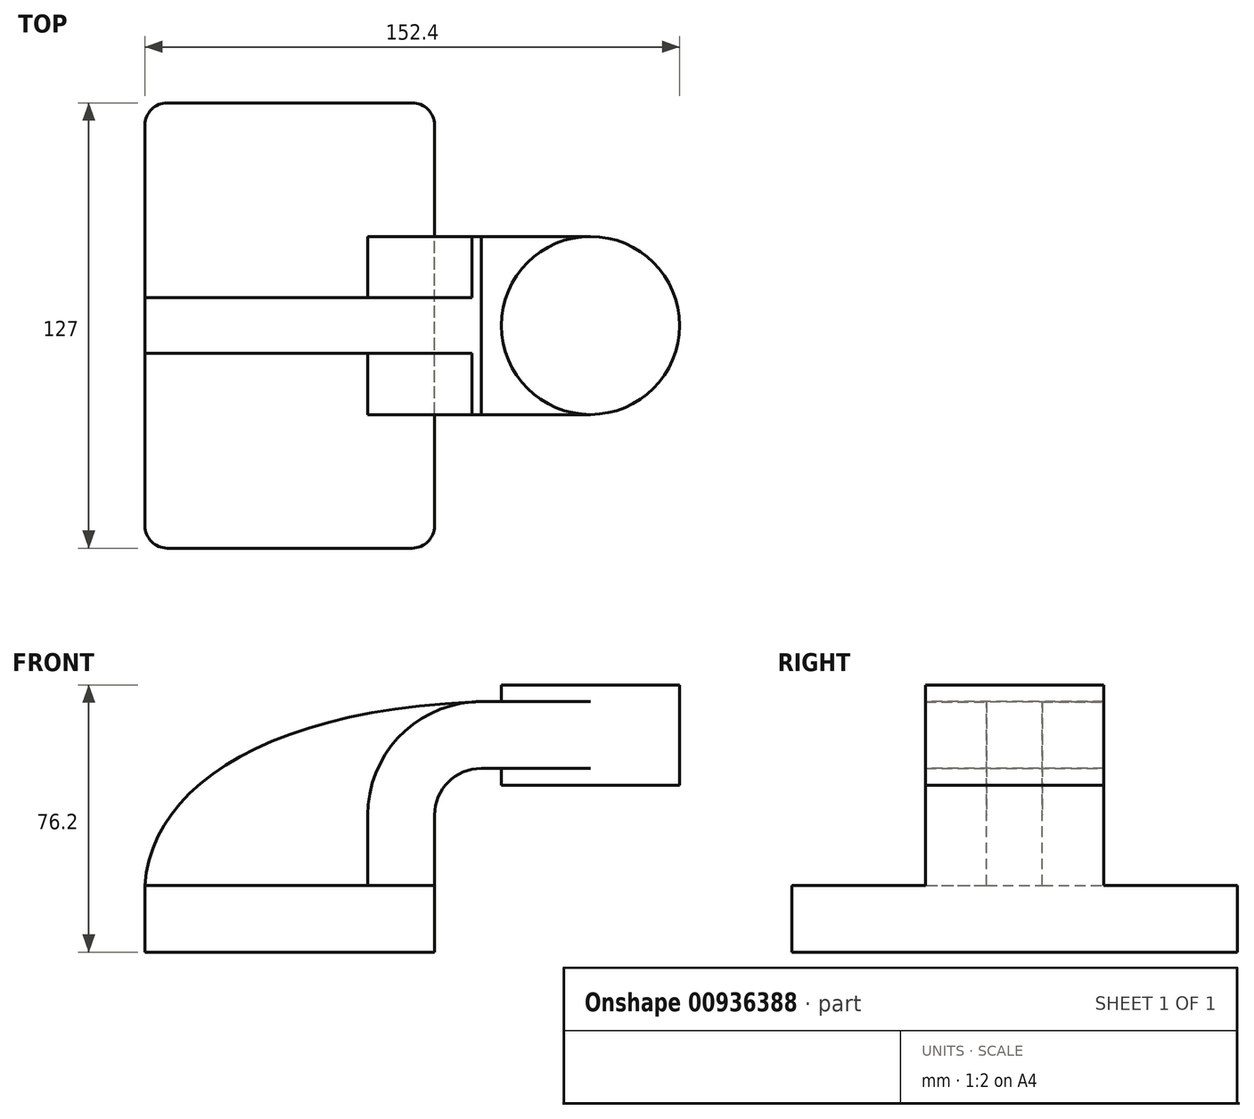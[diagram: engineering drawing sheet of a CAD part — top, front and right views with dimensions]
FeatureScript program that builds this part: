
annotation { "Feature Type Name" : "Feature", "Feature Type Description" : "" }
export const myFeature = defineFeature(function(context is Context, id is Id, definition is map)
    precondition{}
    {
        {
            var Q0;
            Q0=qCreatedBy(makeId("Front.planeOp"),FACE);
            var sketch = newSketch(context, id + "F0", { "sketchPlane" : qUnion([Q0])});
            skLineSegment(sketch, "E0.bottom", {"start": v(-48.85, 2.3) * mm, "end": v(33.7, 2.3) * mm});
            skLineSegment(sketch, "E0.top", {"start": v(-48.85, -16.74) * mm, "end": v(33.7, -16.74) * mm});
            skLineSegment(sketch, "E0.left", {"start": v(-48.85, 2.3) * mm, "end": v(-48.85, -16.74) * mm});
            skLineSegment(sketch, "E0.right", {"start": v(33.7, 2.3) * mm, "end": v(33.7, -16.74) * mm});
            skLineSegment(sketch, "E1.bottom", {"start": v(52.75, 59.46) * mm, "end": v(103.55, 59.46) * mm});
            skLineSegment(sketch, "E1.top", {"start": v(52.75, 30.88) * mm, "end": v(103.55, 30.88) * mm});
            skLineSegment(sketch, "E1.left", {"start": v(52.75, 59.46) * mm, "end": v(52.75, 30.88) * mm});
            skLineSegment(sketch, "E1.right", {"start": v(103.55, 59.46) * mm, "end": v(103.55, 30.88) * mm});
            skPoint(sketch, "E1.middle", {"position": v(78.15, 45.17) * mm});
            skLineSegment(sketch, "E2", {"start": v(33.7, 2.3) * mm, "end": v(33.7, 22.3) * mm});
            skArc(sketch, "E3", {"start": v(33.7, 22.3) * mm, "mid": v(37.61, 31.74) * mm, "end": v(47.06, 35.66) * mm});
            skLineSegment(sketch, "E4", {"start": v(47.06, 35.66) * mm, "end": v(78.15, 35.66) * mm});
            skLineSegment(sketch, "E5.0", {"start": v(47.06, 54.7) * mm, "end": v(78.15, 54.7) * mm});
            skArc(sketch, "E5.1", {"start": v(14.65, 22.3) * mm, "mid": v(24.14, 45.21) * mm, "end": v(47.06, 54.7) * mm});
            skLineSegment(sketch, "E5.2", {"start": v(14.65, 2.3) * mm, "end": v(14.65, 22.3) * mm});
            skLineSegment(sketch, "E6", {"start": v(78.15, 59.46) * mm, "end": v(78.15, 30.88) * mm});
            skFitSpline(sketch, "E7", {"points": [v(-48.85, 2.3) * mm, v(47.06, 54.7) * mm], "startDerivative": vector(6, 84.7) * mm, "endDerivative": vector(184.17, 6.79) * mm});
            skSolve(sketch);
        }
        {
            var Q0;
            Q0=makeQuery(id+"F0.imprint","IMPRINT",FACE,{"disambiguationData":[TD([[makeQuery(id+"F0.imprint","IMPRINT",EDGE,{"derivedFrom":sQuery(id+"F0.wireOp",EDGE,"E0.top")}),1.0]])]});
            extrude(context, id + "F1", {"entities" : qUnion([Q0]), "depth" : 127 * mm, "offsetDistance" : 25.4 * mm, "symmetric" : true});
        }
        {
            var Q0;
            {var subQ1=sQuery(id+"F0.wireOp",EDGE,"E2");Q0=makeQuery(id+"F0.imprint","IMPRINT",FACE,{"disambiguationData":[TD([[makeQuery(id+"F0.imprint","IMPRINT",EDGE,{"derivedFrom":subQ1}),1.0]])]});}
            var Q1;
            {var subQ0=sQuery(id+"F0.wireOp",EDGE,"E5.0");var subQ1=sQuery(id+"F0.wireOp",EDGE,"E1.left");var subQ2=makeQuery(id+"F0.imprint","INTERSECT",VERTEX,{"derivedFrom":[subQ1,subQ0]});Q1=makeQuery(id+"F0.imprint","IMPRINT",FACE,{"disambiguationData":[TD([[makeQuery(id+"F0.imprint","IMPRINT",EDGE,{"disambiguationData":[TD([[subQ2,-1.0]])],"derivedFrom":subQ1}),1.0]])]});}
            extrude(context, id + "F2", {"entities" : qUnion([Q0, Q1]), "operationType" : NewBodyOperationType.ADD, "depth" : 50.8 * mm, "offsetDistance" : 25.4 * mm, "symmetric" : true});
        }
        {
            var Q0;
            {var subQ3=sQuery(id+"F0.wireOp",EDGE,"E5.2");Q0=makeQuery(id+"F0.imprint","IMPRINT",FACE,{"disambiguationData":[TD([[makeQuery(id+"F0.imprint","IMPRINT",EDGE,{"derivedFrom":subQ3}),1.0]])]});}
            extrude(context, id + "F3", {"entities" : qUnion([Q0]), "operationType" : NewBodyOperationType.ADD, "depth" : 15.88 * mm, "offsetDistance" : 25.4 * mm, "symmetric" : true});
        }
        {
            var Q0;
            {var subQ4=sQuery(id+"F0.wireOp",EDGE,"E1.right");Q0=makeQuery(id+"F0.imprint","IMPRINT",FACE,{"disambiguationData":[TD([[makeQuery(id+"F0.imprint","IMPRINT",EDGE,{"derivedFrom":subQ4}),-1.0]])]});}
            var Q1;
            Q1=sQuery(id+"F0.wireOp",EDGE,"E6");
            revolve(context, id + "F4", {"operationType" : NewBodyOperationType.ADD, "surfaceOperationType" : NewSurfaceOperationType.NEW, "entities" : qUnion([Q0]), "axis" : qUnion([Q1]), "revolveType" : RevolveType.FULL});
        }
        {
            var Q0;
            Q0=makeQuery(id+"F1.opExtrude","CAP_EDGE",EDGE,{"disambiguationData":[OSD([sQuery(id+"F0.wireOp",EDGE,"E0.right")])],"isStart":false});
            var Q1;
            Q1=makeQuery(id+"F1.opExtrude","CAP_EDGE",EDGE,{"disambiguationData":[OSD([sQuery(id+"F0.wireOp",EDGE,"E0.left")])],"isStart":false});
            var Q2;
            Q2=makeQuery(id+"F1.opExtrude","CAP_EDGE",EDGE,{"disambiguationData":[OSD([sQuery(id+"F0.wireOp",EDGE,"E0.right")])],"isStart":true});
            var Q3;
            Q3=makeQuery(id+"F1.opExtrude","CAP_EDGE",EDGE,{"disambiguationData":[OSD([sQuery(id+"F0.wireOp",EDGE,"E0.left")])],"isStart":true});
            fillet(context, id + "F5", {"entities" : qUnion([Q0, Q1, Q2, Q3]), "radius" : 6.35 * mm, "tangentPropagation" : true, "allowEdgeOverflow" : false});
        }
    });
